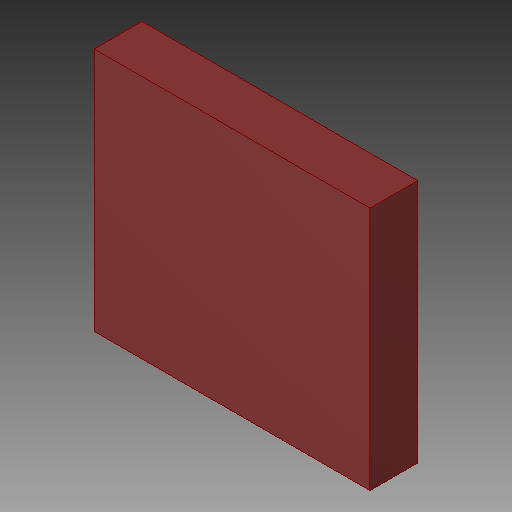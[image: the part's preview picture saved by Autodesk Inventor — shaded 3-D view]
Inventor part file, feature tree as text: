
AUTODESK INVENTOR PART (.ipt)
format: ipt  version: 2019 (Build 230136000, 136)  size: 90,112 bytes
history: native  units: in
note: dims shown in document units (in); Inventor stores cm internally (conversion verified against a paired STEP export)
features: extrude x1, other x1
ambient origin geometry x8: Origin, YZ Plane, XZ Plane, XY Plane, X Axis, Y Axis, Z Axis, Center Point
bodies: Solid1 (feature_tree)
feature tree (2):
  extrude  "Extrusion1"  Depth=0.0394in TaperAngle=0.0deg
  other  "LED5MMRGB, RGBLED_CA-5MM_21"
